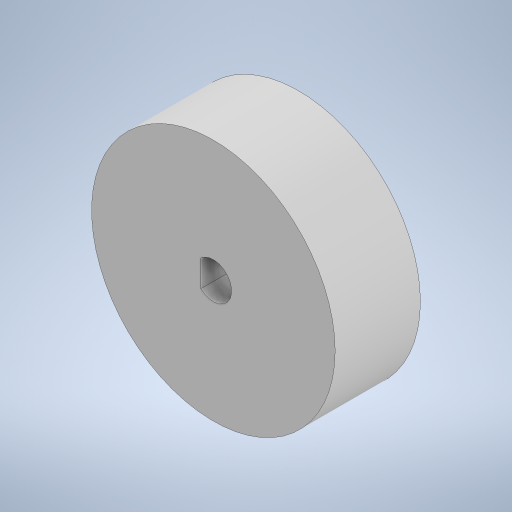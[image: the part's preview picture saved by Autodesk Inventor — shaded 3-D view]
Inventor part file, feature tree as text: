
AUTODESK INVENTOR PART (.ipt)
format: ipt  version: 2023.5 (Build 275446000, 446)  size: 210,944 bytes
history: native  units: mm
features: extrude x2, sketch x2, other x1
ambient origin geometry x8: Origin, YZ Plane, XZ Plane, XY Plane, X Axis, Y Axis, Z Axis, Center Point
bodies: Body1 (feature_tree)
feature tree (5):
  other  "Bryła1"
  extrude  "Wyciągnięcie proste1"  Depth=20.0mm
  extrude  "Wyciągnięcie proste2"  Depth=7.0mm TaperAngle=0.0deg
  sketch  "Szkic1"
  sketch  "Szkic2"
